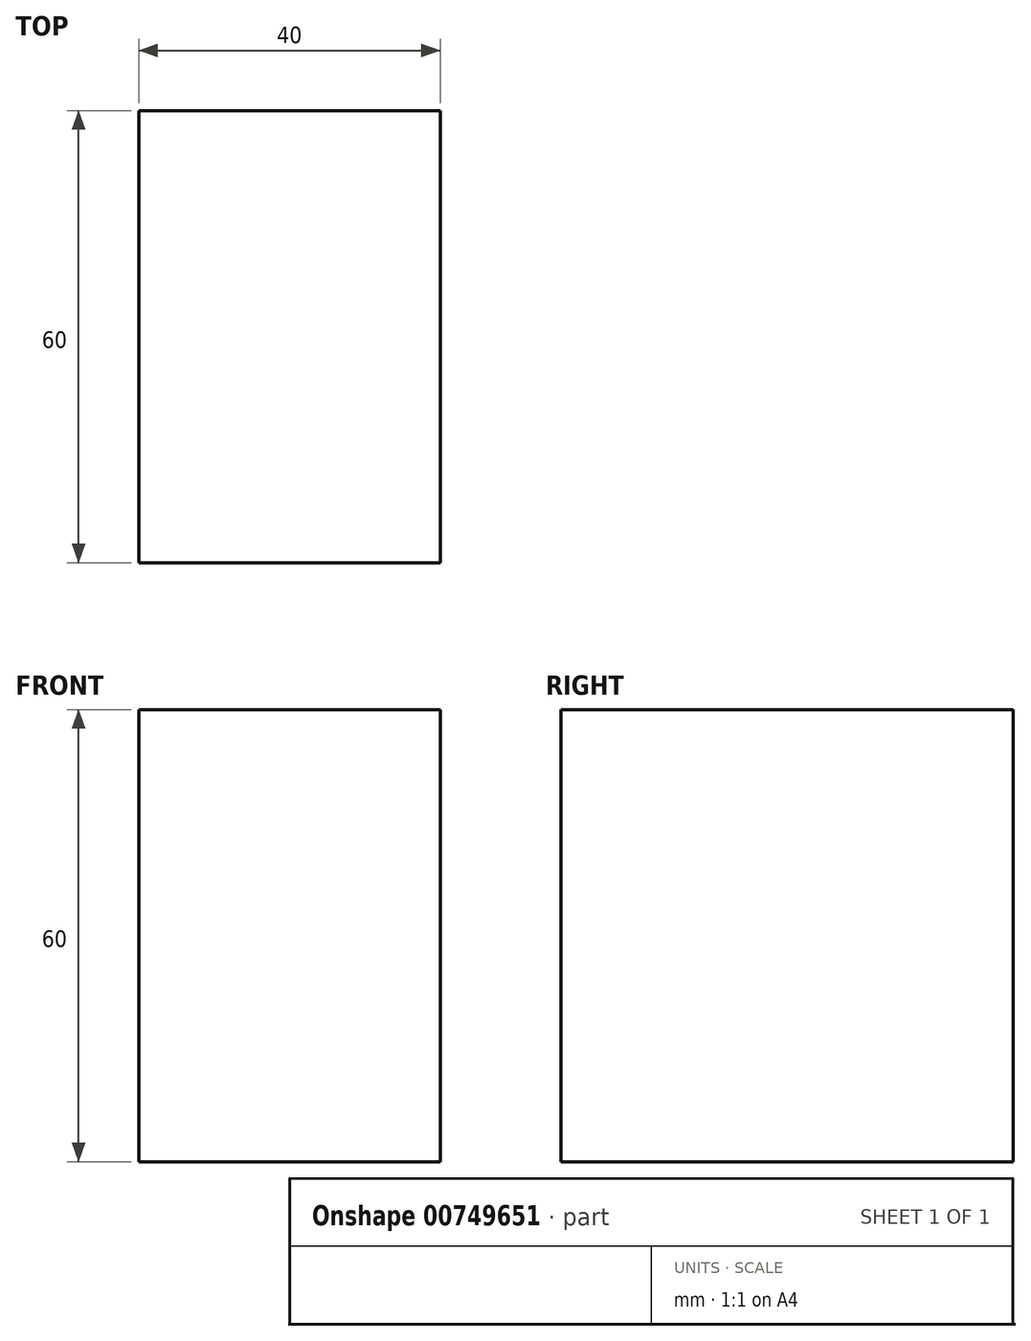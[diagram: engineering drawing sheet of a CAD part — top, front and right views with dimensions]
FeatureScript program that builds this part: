
annotation { "Feature Type Name" : "Feature", "Feature Type Description" : "" }
export const myFeature = defineFeature(function(context is Context, id is Id, definition is map)
    precondition{}
    {
        {
            var Q0;
            Q0=qCreatedBy(makeId("Front.planeOp"),FACE);
            var sketch = newSketch(context, id + "F0", { "sketchPlane" : qUnion([Q0])});
            skLineSegment(sketch, "E0.bottom", {"start": v(0, 0) * mm, "end": v(-40, 0) * mm});
            skLineSegment(sketch, "E0.top", {"start": v(0, -60) * mm, "end": v(-40, -60) * mm});
            skLineSegment(sketch, "E0.left", {"start": v(0, 0) * mm, "end": v(0, -60) * mm});
            skLineSegment(sketch, "E0.right", {"start": v(-40, 0) * mm, "end": v(-40, -60) * mm});
            skSolve(sketch);
        }
        {
            var Q0;
            Q0 = qSketchRegion(id + "F0", true);
            extrude(context, id + "F1", {"entities" : qUnion([Q0]), "depth" : 60 * mm, "offsetDistance" : 25 * mm});
        }
    });
